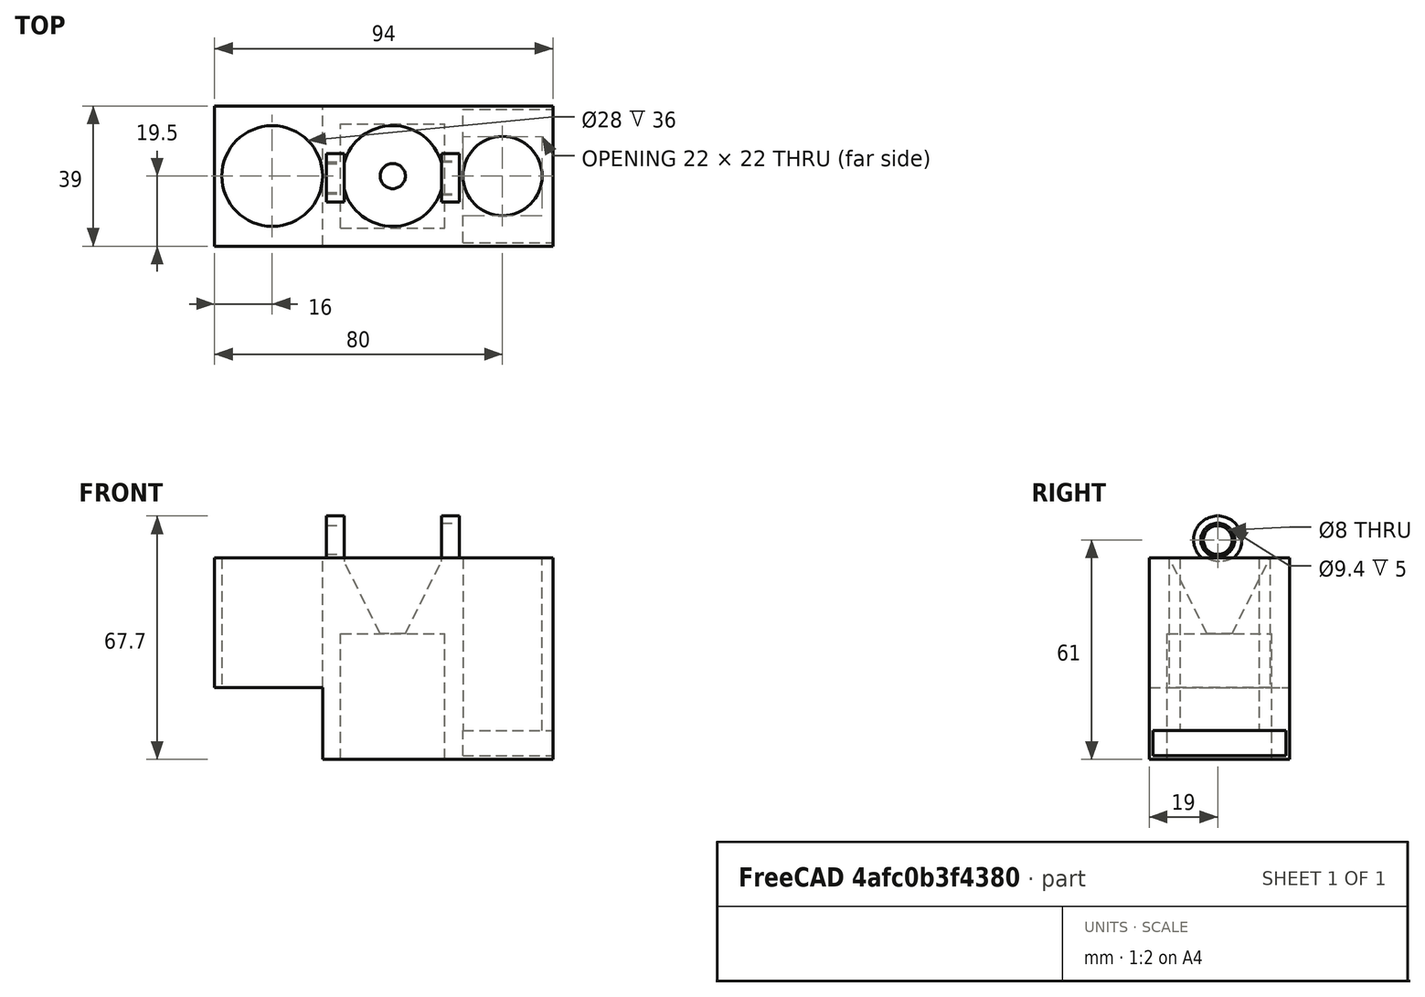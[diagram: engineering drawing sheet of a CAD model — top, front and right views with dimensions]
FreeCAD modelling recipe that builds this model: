
FCSTD DOCUMENT  (FreeCAD 0.21R33771 (Git))
Label: WIP
License: All rights reserved
LicenseURL: https://en.wikipedia.org/wiki/All_rights_reserved
objects: Part::Box×6, Part::Cut×6, Part::FeaturePython×3, Part::Cylinder×2, Part::Cone×1
note: 18 computed .brp shape members not serialized (recipe doc carries the construction recipe); baked Part::Feature solids carry a one-line shape summary decoded from their .brp

FEATURE [Part::Cone] Cone
  Angle = 360
  AttacherType = Attacher::AttachEngine3D
  Height = 21
  Placement = pos=(19.5,19.5,35) rot=(0,0,1;0rad)
  Radius1 = 3.5
  Radius2 = 14
FEATURE [Part::Box] Box  label="Cube"
  AttacherType = Attacher::AttachEngine3D
  Height = 56
  Length = 39
  Width = 39
FEATURE [Part::Box] Box001  label="Cube001"
  AttacherType = Attacher::AttachEngine3D
  Height = 35
  Length = 29
  Placement = pos=(5,5,0) rot=(0,0,1;0rad)
  Width = 29
FEATURE [Part::Box] Box002  label="Cube002"
  AttacherType = Attacher::AttachEngine3D
  Height = 56
  Length = 25
  Placement = pos=(39,0,0) rot=(0,0,1;0rad)
  Width = 39
FEATURE [Part::Cut] Cut
  Base = -> Box
  Tool = -> Cone
FEATURE [Part::Cut] Cut001
  Base = -> Cut
  Tool = -> Box001
FEATURE [Part::Box] Box003  label="Cube003"
  AttacherType = Attacher::AttachEngine3D
  Height = 56
  Length = 30
  Placement = pos=(-30,0,0) rot=(0,0,1;0rad)
  Width = 39
FEATURE [Part::FeaturePython] Tube002  # WARN: FeaturePython — macro-defined, semantics opaque (R4)
  AttacherType = Attacher::AttachEngine3D
  Height = 5
  InnerRadius = 4.7
  OuterRadius = 6.7
  Placement = pos=(33,19,61) rot=(0,1,0;1.5708rad)
FEATURE [Part::FeaturePython] Tube003  # WARN: FeaturePython — macro-defined, semantics opaque (R4)
  AttacherType = Attacher::AttachEngine3D
  Height = 5
  InnerRadius = 4
  OuterRadius = 6.7
  Placement = pos=(1,19,61) rot=(0,1,0;1.5708rad)
FEATURE [Part::Cylinder] Cylinder
  Angle = 360
  AttacherType = Attacher::AttachEngine3D
  FirstAngle = 0
  Height = 55
  Placement = pos=(50,19.5,1) rot=(0,0,1;0rad)
  Radius = 11
  SecondAngle = 0
FEATURE [Part::Cylinder] Cylinder001
  Angle = 360
  AttacherType = Attacher::AttachEngine3D
  FirstAngle = 0
  Height = 55
  Placement = pos=(-14,19.5,1) rot=(0,0,1;0rad)
  Radius = 14
  SecondAngle = 0
FEATURE [Part::Cut] Cut002
  Base = -> Box002
  Tool = -> Cylinder
FEATURE [Part::Cut] Cut003
  Base = -> Box003
  Tool = -> Cylinder001
FEATURE [Part::Box] Box004  label="Cube004"
  AttacherType = Attacher::AttachEngine3D
  Height = 20
  Length = 30
  Placement = pos=(-30,0,0) rot=(0,0,1;0rad)
  Width = 39
FEATURE [Part::Cut] Cut004
  Base = -> Cut003
  Tool = -> Box004
FEATURE [Part::Box] Box005  label="Cube005"
  AttacherType = Attacher::AttachEngine3D
  Height = 7
  Length = 25
  Placement = pos=(39,1,1) rot=(0,0,1;0rad)
  Width = 37
FEATURE [Part::Cut] Cut005
  Base = -> Cut002
  Tool = -> Box005
FEATURE [Part::FeaturePython] Connect  # WARN: FeaturePython — macro-defined, semantics opaque (R4)
  Objects = -> [Cut001,Tube002,Cut,Box001,Tube003,Cut004,Cut005]
  Tolerance = 0
